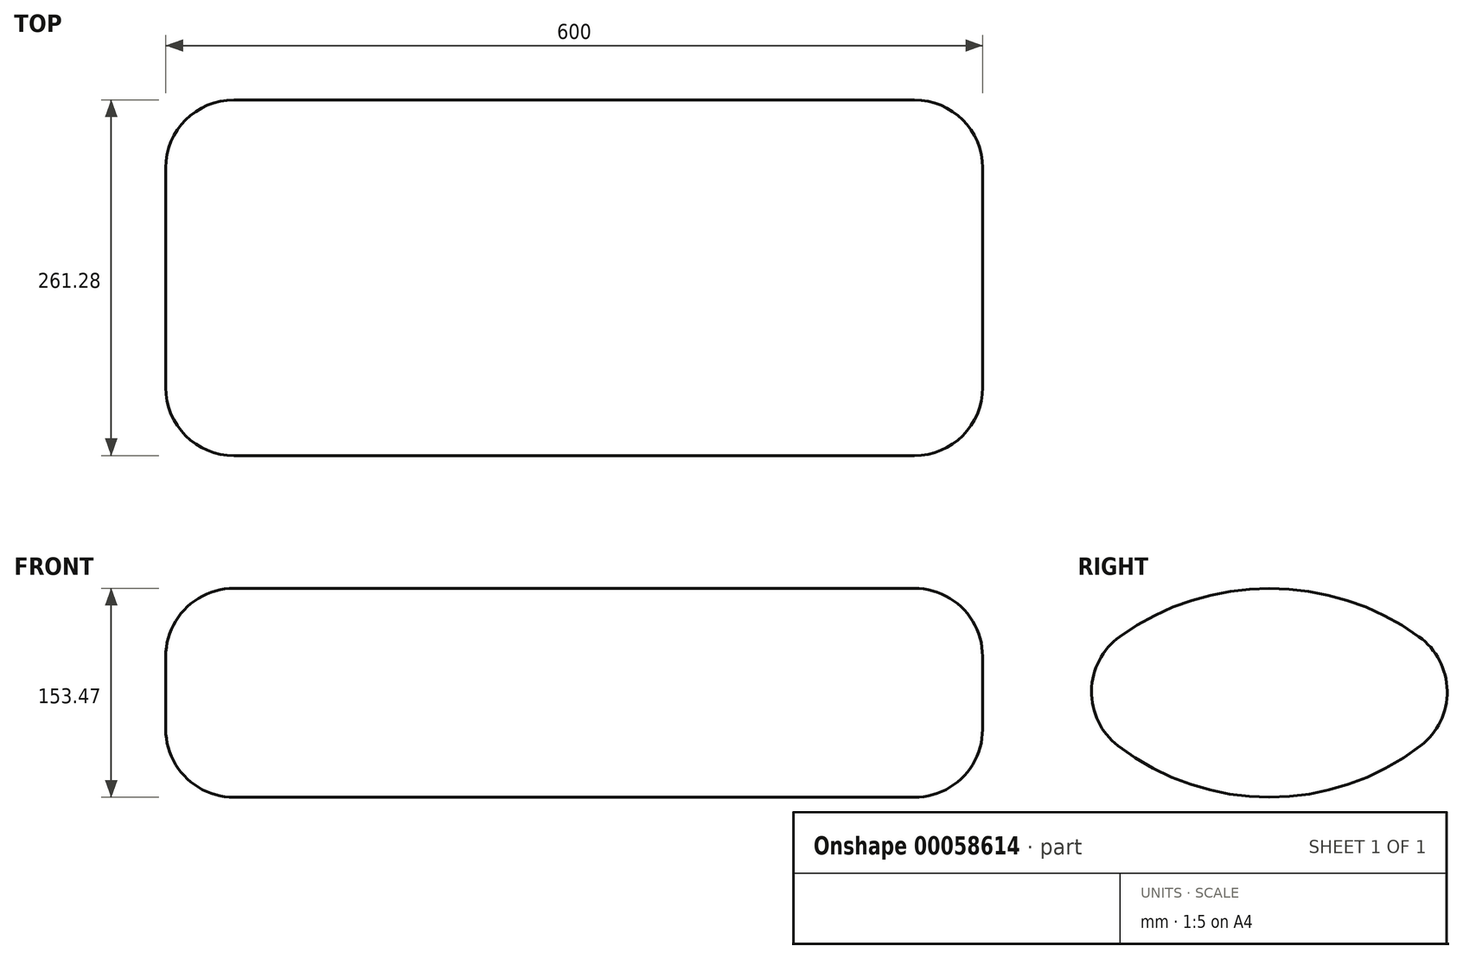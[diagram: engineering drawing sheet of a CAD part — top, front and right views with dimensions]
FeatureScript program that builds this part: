
annotation { "Feature Type Name" : "Feature", "Feature Type Description" : "" }
export const myFeature = defineFeature(function(context is Context, id is Id, definition is map)
    precondition{}
    {
        {
            var Q0;
            Q0=qCreatedBy(makeId("Right.planeOp"),FACE);
            var sketch = newSketch(context, id + "F0", { "sketchPlane" : qUnion([Q0])});
            skArc(sketch, "E0", {"start": v(300, 0) * mm, "mid": v(150, 74.75) * mm, "end": v(0, 0) * mm});
            skArc(sketch, "E1", {"start": v(0, 0) * mm, "mid": v(150, -78.72) * mm, "end": v(300, 0) * mm});
            skSolve(sketch);
        }
        {
            var Q0;
            Q0 = qSketchRegion(id + "F0", true);
            extrude(context, id + "F1", {"entities" : qUnion([Q0]), "depth" : 600 * mm});
        }
        {
            var Q0;
            {var subQ0=sQuery(id+"F0.wireOp",EDGE,"E1");var subQ1=sQuery(id+"F0.wireOp",EDGE,"E0");Q0=makeQuery(id+"F1.opExtrude","SWEPT_EDGE",EDGE,{"disambiguationData":[OSD([subQ1,subQ0]),TDD([makeQuery(id+"F0.imprint","INTERSECT",VERTEX,{"disambiguationData":[OD(1.0)],"derivedFrom":[subQ1,subQ0]})])]});}
            var Q1;
            {var subQ0=sQuery(id+"F0.wireOp",EDGE,"E1");var subQ1=sQuery(id+"F0.wireOp",EDGE,"E0");Q1=makeQuery(id+"F1.opExtrude","SWEPT_EDGE",EDGE,{"disambiguationData":[OSD([subQ1,subQ0]),TDD([makeQuery(id+"F0.imprint","INTERSECT",VERTEX,{"disambiguationData":[OD(0.0)],"derivedFrom":[subQ1,subQ0]})])]});}
            fillet(context, id + "F2", {"entities" : qUnion([Q0, Q1]), "radius" : 50 * mm, "tangentPropagation" : true, "allowEdgeOverflow" : false});
        }
        {
            var Q0;
            Q0=makeQuery(id+"F1.opExtrude","CAP_FACE",FACE,{"disambiguationData":[OSD([sQuery(id+"F0.wireOp",EDGE,"E0"),sQuery(id+"F0.wireOp",EDGE,"E1")])],"isStart":false});
            var Q1;
            Q1=makeQuery(id+"F1.opExtrude","CAP_FACE",FACE,{"disambiguationData":[OSD([sQuery(id+"F0.wireOp",EDGE,"E0"),sQuery(id+"F0.wireOp",EDGE,"E1")])],"isStart":true});
            fillet(context, id + "F3", {"entities" : qUnion([Q0, Q1]), "radius" : 50 * mm, "tangentPropagation" : true, "allowEdgeOverflow" : false});
        }
    });
